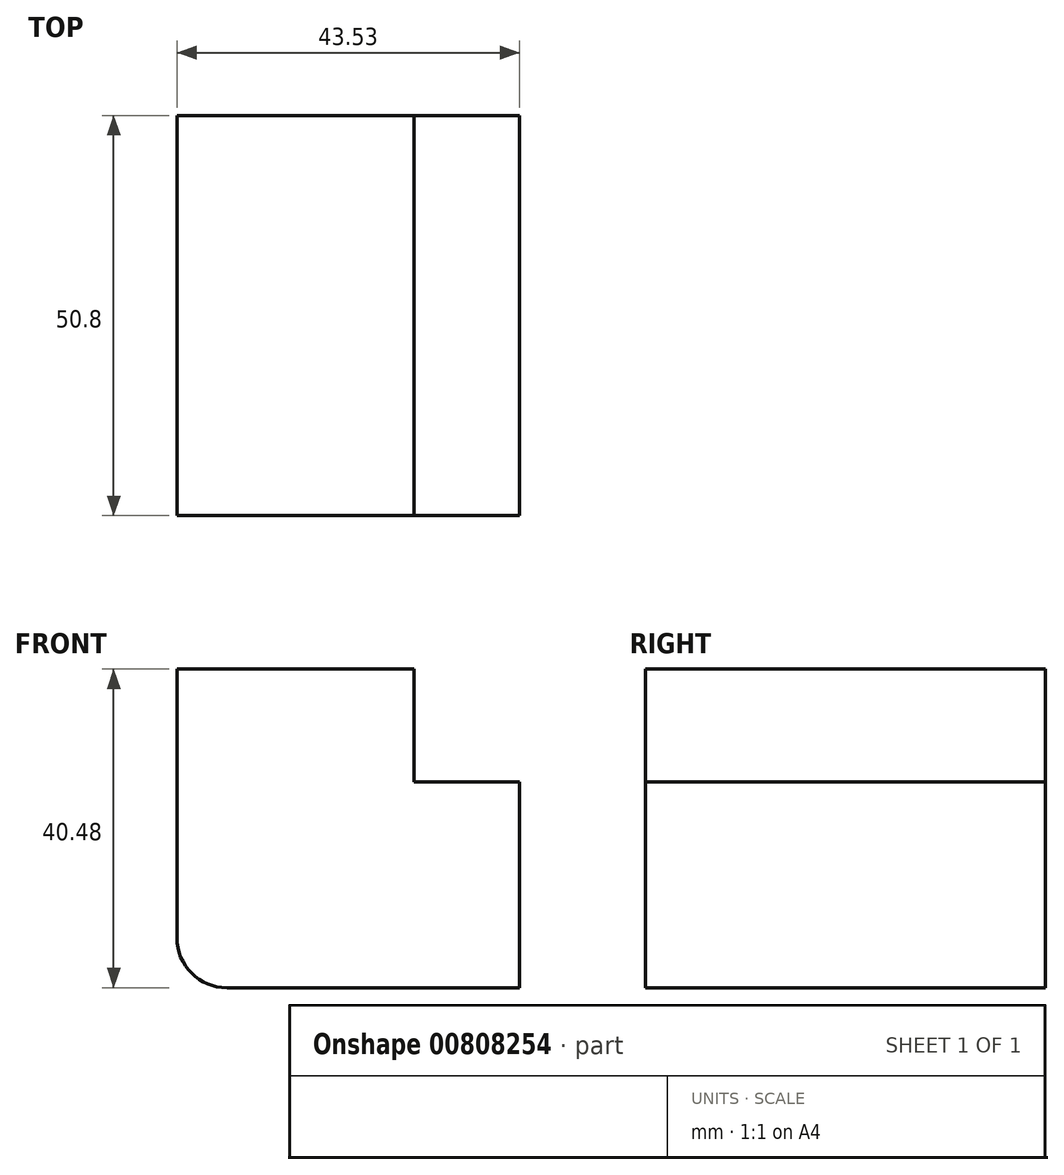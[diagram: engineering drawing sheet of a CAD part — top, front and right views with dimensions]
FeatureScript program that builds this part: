
annotation { "Feature Type Name" : "Feature", "Feature Type Description" : "" }
export const myFeature = defineFeature(function(context is Context, id is Id, definition is map)
    precondition{}
    {
        {
            var Q0;
            Q0=qCreatedBy(makeId("Front.planeOp"),FACE);
            var sketch = newSketch(context, id + "F0", { "sketchPlane" : qUnion([Q0])});
            skLineSegment(sketch, "E0.bottom", {"start": v(6.35, 0) * mm, "end": v(43.53, 0) * mm});
            skLineSegment(sketch, "E0.top", {"start": v(0, 40.48) * mm, "end": v(43.53, 40.48) * mm});
            skLineSegment(sketch, "E0.left", {"start": v(0, 6.35) * mm, "end": v(0, 40.48) * mm});
            skLineSegment(sketch, "E0.right", {"start": v(43.53, 0) * mm, "end": v(43.53, 40.48) * mm});
            skLineSegment(sketch, "E1.bottom", {"start": v(43.53, 40.48) * mm, "end": v(30.13, 40.48) * mm});
            skLineSegment(sketch, "E1.top", {"start": v(43.53, 26.13) * mm, "end": v(30.13, 26.13) * mm});
            skLineSegment(sketch, "E1.left", {"start": v(43.53, 40.48) * mm, "end": v(43.53, 26.13) * mm});
            skLineSegment(sketch, "E1.right", {"start": v(30.13, 40.48) * mm, "end": v(30.13, 26.13) * mm});
            skPoint(sketch, "E2.visualSharp", {"position": v(0, 0) * mm});
            skArc(sketch, "E2.filletArc", {"start": v(0, 6.35) * mm, "mid": v(1.86, 1.86) * mm, "end": v(6.35, 0) * mm});
            skSolve(sketch);
        }
        {
            var Q0;
            Q0=makeQuery(id+"F0.imprint","IMPRINT",FACE,{"disambiguationData":[TD([[makeQuery(id+"F0.imprint","IMPRINT",EDGE,{"derivedFrom":sQuery(id+"F0.wireOp",EDGE,"E0.bottom")}),1.0]])]});
            extrude(context, id + "F1", {"entities" : qUnion([Q0]), "depth" : 50.8 * mm, "offsetDistance" : 25.4 * mm});
        }
    });
